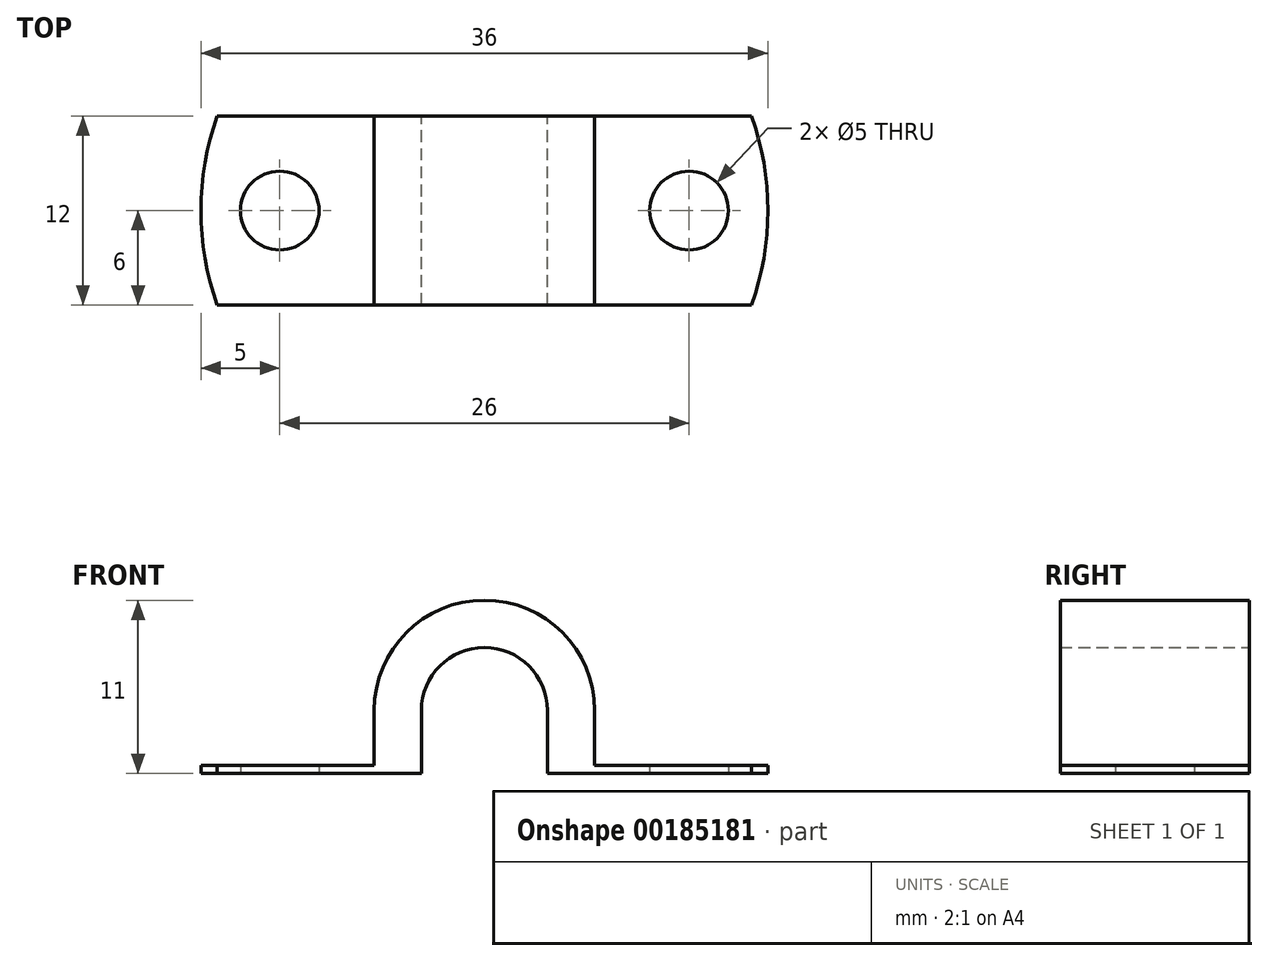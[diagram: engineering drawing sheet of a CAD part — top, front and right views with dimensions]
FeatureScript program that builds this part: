
annotation { "Feature Type Name" : "Feature", "Feature Type Description" : "" }
export const myFeature = defineFeature(function(context is Context, id is Id, definition is map)
    precondition{}
    {
        {
            var Q0;
            Q0=qCreatedBy(makeId("Front.planeOp"),FACE);
            var sketch = newSketch(context, id + "F0", { "sketchPlane" : qUnion([Q0])});
            skLineSegment(sketch, "E0", {"start": v(0, 6.94) * mm, "end": v(0, -7.1) * mm, "construction": true});
            skArc(sketch, "E1", {"start": v(4, 4) * mm, "mid": v(0, 8) * mm, "end": v(-4, 4) * mm});
            skArc(sketch, "E2", {"start": v(7, 4) * mm, "mid": v(0, 11) * mm, "end": v(-7, 4) * mm});
            skLineSegment(sketch, "E3", {"start": v(-4, 0) * mm, "end": v(-18, 0) * mm});
            skLineSegment(sketch, "E4", {"start": v(-18, 0) * mm, "end": v(-18, 0.5) * mm});
            skLineSegment(sketch, "E5", {"start": v(-7, 4) * mm, "end": v(-7, 0.5) * mm});
            skLineSegment(sketch, "E6", {"start": v(-7, 0.5) * mm, "end": v(-18, 0.5) * mm});
            skLineSegment(sketch, "E7", {"start": v(-4, 4) * mm, "end": v(-4, 0) * mm});
            skLineSegment(sketch, "E8.MirrorCS", {"start": v(18, 0) * mm, "end": v(18, 0.5) * mm});
            skLineSegment(sketch, "E9.MirrorCS", {"start": v(7, 4) * mm, "end": v(7, 0.5) * mm});
            skLineSegment(sketch, "E10.MirrorCS", {"start": v(7, 0.5) * mm, "end": v(18, 0.5) * mm});
            skLineSegment(sketch, "E11.MirrorCS", {"start": v(4, 4) * mm, "end": v(4, 0) * mm});
            skLineSegment(sketch, "E12.MirrorCS", {"start": v(4, 0) * mm, "end": v(18, 0) * mm});
            skPoint(sketch, "E13.orphan", {"position": v(0, 0) * mm});
            skSolve(sketch);
        }
        {
            var Q0;
            Q0 = qSketchRegion(id + "F0", true);
            extrude(context, id + "F1", {"entities" : qUnion([Q0]), "depth" : 12 * mm});
        }
        {
            var Q0;
            Q0=makeQuery(id+"F1.opExtrude","SWEPT_FACE",FACE,{"disambiguationData":[OSD([sQuery(id+"F0.wireOp",EDGE,"E3")])]});
            var sketch = newSketch(context, id + "F2", { "sketchPlane" : qUnion([Q0])});
            skLineSegment(sketch, "E14", {"start": v(-18, 6) * mm, "end": v(16.1, 6) * mm, "construction": true});
            skLineSegment(sketch, "E15", {"start": v(0, 0) * mm, "end": v(0, 12) * mm, "construction": true});
            skCircle(sketch, "E16", {"center": v(-13, 6) * mm, "radius": 2.5 * mm});
            skCircle(sketch, "E17.MirrorC", {"center": v(13, 6) * mm, "radius": 2.5 * mm});
            skArc(sketch, "E18", {"start": v(-16.97, 12) * mm, "mid": v(-18, 6) * mm, "end": v(-16.97, 0) * mm});
            skLineSegment(sketch, "E19", {"start": v(-16.97, 12) * mm, "end": v(-18, 12) * mm});
            skLineSegment(sketch, "E20", {"start": v(-18, 12) * mm, "end": v(-18, 0) * mm});
            skLineSegment(sketch, "E21", {"start": v(-18, 0) * mm, "end": v(-16.97, 0) * mm});
            skLineSegment(sketch, "E22.MirrorCS", {"start": v(18, 0) * mm, "end": v(16.97, 0) * mm});
            skLineSegment(sketch, "E23.MirrorCS", {"start": v(16.97, 12) * mm, "end": v(18, 12) * mm});
            skLineSegment(sketch, "E24.MirrorCS", {"start": v(18, 12) * mm, "end": v(18, 0) * mm});
            skArc(sketch, "E25.trimOffspring", {"start": v(16.97, 0) * mm, "mid": v(18, 6) * mm, "end": v(16.97, 12) * mm});
            skSolve(sketch);
        }
        {
            var Q0;
            Q0 = qSketchRegion(id + "F2", true);
            extrude(context, id + "F3", {"entities" : qUnion([Q0]), "operationType" : NewBodyOperationType.REMOVE, "oppositeDirection" : true, "depth" : 25 * mm});
        }
    });
